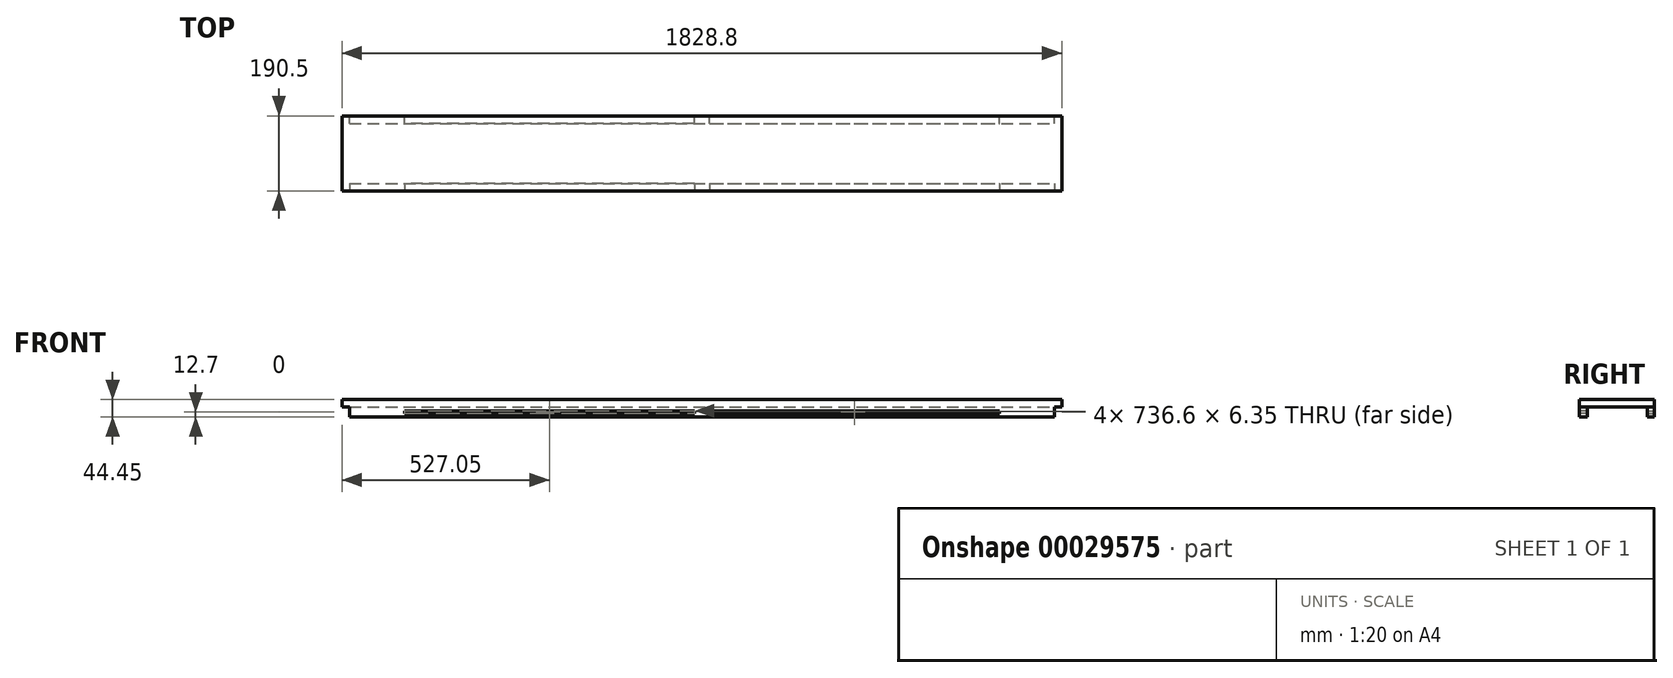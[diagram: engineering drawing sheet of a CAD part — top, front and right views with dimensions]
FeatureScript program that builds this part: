
annotation { "Feature Type Name" : "Feature", "Feature Type Description" : "" }
export const myFeature = defineFeature(function(context is Context, id is Id, definition is map)
    precondition{}
    {
        {
            var Q0;
            Q0=qCreatedBy(makeId("Top.planeOp"),FACE);
            var sketch = newSketch(context, id + "F0", { "sketchPlane" : qUnion([Q0])});
            skLineSegment(sketch, "E0.rect.bottom", {"start": v(-914.4, -95.25) * mm, "end": v(914.4, -95.25) * mm});
            skLineSegment(sketch, "E0.rect.top", {"start": v(-914.4, 95.25) * mm, "end": v(914.4, 95.25) * mm});
            skLineSegment(sketch, "E0.rect.left", {"start": v(-914.4, -95.25) * mm, "end": v(-914.4, 95.25) * mm});
            skLineSegment(sketch, "E0.rect.right", {"start": v(914.4, -95.25) * mm, "end": v(914.4, 95.25) * mm});
            skPoint(sketch, "E0.rect.middle", {"position": v(0, 0) * mm});
            skSolve(sketch);
        }
        {
            var Q0;
            Q0=makeQuery(id+"F0.imprint","IMPRINT",FACE,{"disambiguationData":[TD([[makeQuery(id+"F0.imprint","IMPRINT",EDGE,{"derivedFrom":sQuery(id+"F0.wireOp",EDGE,"E0.rect.bottom")}),1.0]])]});
            extrude(context, id + "F1", {"entities" : qUnion([Q0]), "depth" : 19.05 * mm});
        }
        {
            var Q0;
            Q0=makeQuery(id+"F1.opExtrude","CAP_FACE",FACE,{"disambiguationData":[OSD([sQuery(id+"F0.wireOp",EDGE,"E0.rect.bottom"),sQuery(id+"F0.wireOp",EDGE,"E0.rect.top"),sQuery(id+"F0.wireOp",EDGE,"E0.rect.left"),sQuery(id+"F0.wireOp",EDGE,"E0.rect.right")])],"isStart":true});
            var sketch = newSketch(context, id + "F2", { "sketchPlane" : qUnion([Q0])});
            skLineSegment(sketch, "E1.rect.bottom", {"start": v(-895.35, 76.2) * mm, "end": v(895.35, 76.2) * mm});
            skLineSegment(sketch, "E1.rect.top", {"start": v(-895.35, -76.2) * mm, "end": v(895.35, -76.2) * mm});
            skLineSegment(sketch, "E1.rect.left", {"start": v(-895.35, 76.2) * mm, "end": v(-895.35, -76.2) * mm});
            skLineSegment(sketch, "E1.rect.right", {"start": v(895.35, 76.2) * mm, "end": v(895.35, -76.2) * mm});
            skPoint(sketch, "E1.rect.middle", {"position": v(0, 0) * mm});
            skLineSegment(sketch, "E2", {"start": v(-895.35, 76.2) * mm, "end": v(-895.35, 95.25) * mm});
            skLineSegment(sketch, "E3", {"start": v(-895.35, -76.2) * mm, "end": v(-895.35, -95.25) * mm});
            skLineSegment(sketch, "E4", {"start": v(895.35, -76.2) * mm, "end": v(895.35, -95.25) * mm});
            skLineSegment(sketch, "E5", {"start": v(895.35, 76.2) * mm, "end": v(895.35, 95.25) * mm});
            skSolve(sketch);
        }
        {
            var Q0;
            Q0=makeQuery(id+"F2.imprint","IMPRINT",FACE,{"disambiguationData":[TD([[makeQuery(id+"F2.imprint","IMPRINT",EDGE,{"derivedFrom":sQuery(id+"F2.wireOp",EDGE,"E1.rect.bottom")}),1.0]])]});
            var Q1;
            Q1=makeQuery(id+"F2.imprint","IMPRINT",FACE,{"disambiguationData":[TD([[makeQuery(id+"F2.imprint","IMPRINT",EDGE,{"derivedFrom":sQuery(id+"F2.wireOp",EDGE,"E1.rect.top")}),-1.0]])]});
            extrude(context, id + "F3", {"entities" : qUnion([Q0, Q1]), "operationType" : NewBodyOperationType.ADD, "depth" : 25.4 * mm});
        }
        {
            var Q0;
            {var subQ0=sQuery(id+"F0.wireOp",EDGE,"E0.rect.bottom");Q0=makeQuery(id+"F3.boolean.opBoolean","MERGE",FACE,{"derivedFrom":[makeQuery(id+"F1.opExtrude","SWEPT_FACE",FACE,{"disambiguationData":[OSD([subQ0])]}),makeQuery(id+"F3.opExtrude","SWEPT_FACE",FACE,{"disambiguationData":[OSD([subQ0])]})]});}
            var sketch = newSketch(context, id + "F4", { "sketchPlane" : qUnion([Q0])});
            skPoint(sketch, "E6", {"position": v(-895.35, -12.7) * mm});
            skPoint(sketch, "E7", {"position": v(895.35, -12.7) * mm});
            skLineSegment(sketch, "E8.rect.bottom", {"start": v(19.05, -9.52) * mm, "end": v(755.65, -9.52) * mm});
            skLineSegment(sketch, "E8.rect.top", {"start": v(19.05, -15.87) * mm, "end": v(755.65, -15.87) * mm});
            skLineSegment(sketch, "E8.rect.left", {"start": v(19.05, -9.53) * mm, "end": v(19.05, -15.87) * mm});
            skLineSegment(sketch, "E8.rect.right", {"start": v(755.65, -9.53) * mm, "end": v(755.65, -15.87) * mm});
            skPoint(sketch, "E8.rect.middle", {"position": v(0, -12.7) * mm});
            skLineSegment(sketch, "E9", {"start": v(0, 19.05) * mm, "end": v(0, -25.4) * mm, "construction": true});
            skLineSegment(sketch, "E10.MirrorCS", {"start": v(-755.65, -9.53) * mm, "end": v(-755.65, -15.87) * mm});
            skLineSegment(sketch, "E11.MirrorCS", {"start": v(-19.05, -9.53) * mm, "end": v(-19.05, -15.87) * mm});
            skLineSegment(sketch, "E12.MirrorCS", {"start": v(-19.05, -15.87) * mm, "end": v(-755.65, -15.87) * mm});
            skLineSegment(sketch, "E13.MirrorCS", {"start": v(-19.05, -9.52) * mm, "end": v(-755.65, -9.52) * mm});
            skSolve(sketch);
        }
        {
            var Q0;
            Q0=makeQuery(id+"F4.imprint","IMPRINT",FACE,{"disambiguationData":[TD([[makeQuery(id+"F4.imprint","IMPRINT",EDGE,{"derivedFrom":sQuery(id+"F4.wireOp",EDGE,"E8.rect.bottom")}),-1.0]])]});
            var Q1;
            Q1=makeQuery(id+"F4.imprint","IMPRINT",FACE,{"disambiguationData":[TD([[makeQuery(id+"F4.imprint","IMPRINT",EDGE,{"derivedFrom":sQuery(id+"F4.wireOp",EDGE,"E10.MirrorCS")}),1.0]])]});
            extrude(context, id + "F5", {"entities" : qUnion([Q0, Q1]), "operationType" : NewBodyOperationType.REMOVE, "oppositeDirection" : true, "depth" : 19.05 * mm});
        }
        {
            var Q0;
            {var subQ0=sQuery(id+"F0.wireOp",EDGE,"E0.rect.top");Q0=makeQuery(id+"F3.boolean.opBoolean","MERGE",FACE,{"derivedFrom":[makeQuery(id+"F1.opExtrude","SWEPT_FACE",FACE,{"disambiguationData":[OSD([subQ0])]}),makeQuery(id+"F3.opExtrude","SWEPT_FACE",FACE,{"disambiguationData":[OSD([subQ0])]})]});}
            var sketch = newSketch(context, id + "F6", { "sketchPlane" : qUnion([Q0])});
            skLineSegment(sketch, "E14.bottom", {"start": v(-19.05, -9.52) * mm, "end": v(-755.65, -9.52) * mm});
            skLineSegment(sketch, "E14.top", {"start": v(-19.05, -15.87) * mm, "end": v(-755.65, -15.88) * mm});
            skLineSegment(sketch, "E14.left", {"start": v(-19.05, -9.52) * mm, "end": v(-19.05, -15.87) * mm});
            skLineSegment(sketch, "E14.right", {"start": v(-755.65, -9.52) * mm, "end": v(-755.65, -15.88) * mm});
            skLineSegment(sketch, "E15.MirrorCS", {"start": v(755.65, -9.52) * mm, "end": v(755.65, -15.88) * mm});
            skLineSegment(sketch, "E16.MirrorCS", {"start": v(19.05, -9.52) * mm, "end": v(19.05, -15.87) * mm});
            skLineSegment(sketch, "E17.MirrorCS", {"start": v(19.05, -15.87) * mm, "end": v(755.65, -15.88) * mm});
            skLineSegment(sketch, "E18.MirrorCS", {"start": v(19.05, -9.52) * mm, "end": v(755.65, -9.52) * mm});
            skSolve(sketch);
        }
        {
            var Q0;
            Q0=makeQuery(id+"F6.imprint","IMPRINT",FACE,{"disambiguationData":[TD([[makeQuery(id+"F6.imprint","IMPRINT",EDGE,{"derivedFrom":sQuery(id+"F6.wireOp",EDGE,"E14.bottom")}),1.0]])]});
            var Q1;
            Q1=makeQuery(id+"F6.imprint","IMPRINT",FACE,{"disambiguationData":[TD([[makeQuery(id+"F6.imprint","IMPRINT",EDGE,{"derivedFrom":sQuery(id+"F6.wireOp",EDGE,"E16.MirrorCS")}),1.0]])]});
            extrude(context, id + "F7", {"entities" : qUnion([Q0, Q1]), "operationType" : NewBodyOperationType.REMOVE, "oppositeDirection" : true, "depth" : 19.05 * mm});
        }
    });
